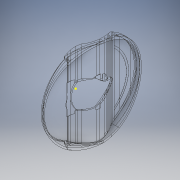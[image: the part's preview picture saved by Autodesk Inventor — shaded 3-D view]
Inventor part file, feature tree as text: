
AUTODESK INVENTOR PART (.ipt)
format: ipt  version: 2018 (Build 220112000, 112)  size: 1,359,360 bytes
history: native  units: mm
features: sketch x50, extrude x43, fillet x2, revolve x1, mirror x1
ambient origin geometry x8: Origin, YZ Plane, XZ Plane, XY Plane, X Axis, Y Axis, Z Axis, Center Point
bodies: Solid1 (feature_tree)
feature tree (97):
  extrude  "Extrusion1"  TaperAngle=0.0deg  [1 undecoded]
  extrude  "Extrusion2"  Depth=10.0mm TaperAngle=0.0deg
  extrude  "Extrusion3"  Depth=10.0mm
  extrude  "Extrusion4"  TaperAngle=0.0deg  [1 undecoded]
  extrude  "Extrusion5"  Depth=10.0mm TaperAngle=0.0deg
  sketch  "Sketch6"  dims[d19=10.0mm d20=0.0mm d21=40.0mm]
  extrude  "Extrusion6"  Depth=10.0mm
  extrude  "Extrusion7"  Depth=11.0mm TaperAngle=0.0deg
  extrude  "Extrusion8"  Depth=32.0mm TaperAngle=0.0deg
  extrude  "Extrusion9"  Depth=32.0mm TaperAngle=0.0deg
  extrude  "Extrusion10"  Depth=10.0mm TaperAngle=0.0deg
  extrude  "Extrusion11"  Depth=10.0mm TaperAngle=0.0deg
  extrude  "Extrusion12"  TaperAngle=0.0deg  [1 undecoded]
  extrude  "Extrusion14"  Depth=48.3mm
  extrude  "Extrusion15"  TaperAngle=0.0deg  [1 undecoded]
  extrude  "Extrusion16"  Depth=10.0mm TaperAngle=0.0deg
  extrude  "Extrusion17"  Depth=11.63mm TaperAngle=0.0deg
  sketch  "Sketch21"  dims[d83=0.0mm d84=0.0mm d85=0.0mm d86=0.0mm]
  extrude  "Extrusion19"  Depth=11.63mm TaperAngle=0.0deg
  extrude  "Extrusion20"  TaperAngle=0.0deg  [1 undecoded]
  extrude  "Extrusion21"  Depth=10.0mm TaperAngle=0.0deg
  extrude  "Extrusion22"  TaperAngle=0.0deg  [1 undecoded]
  extrude  "Extrusion23"  Depth=2.86mm TaperAngle=0.0deg
  extrude  "Extrusion24"  TaperAngle=0.0deg  [1 undecoded]
  extrude  "Extrusion25"  Depth=2.22mm
  sketch  "Sketch33"  dims[d113=7.8mm d114=0.0mm d115=7.8mm d116=0.0mm]
  extrude  "Extrusion26"  Depth=10.0mm TaperAngle=0.0deg
  extrude  "Extrusion27"  Depth=7.8mm TaperAngle=0.0deg
  extrude  "Extrusion28"  Depth=16.0mm TaperAngle=0.0deg
  extrude  "Extrusion29"  [1 undecoded]
  extrude  "Extrusion30"  [1 undecoded]
  extrude  "Extrusion31"  [1 undecoded]
  extrude  "Extrusion32"  [1 undecoded]
  extrude  "Extrusion33"  [1 undecoded]
  sketch  "Sketch42"
  extrude  "Extrusion34"  [1 undecoded]
  extrude  "Extrusion36"  [1 undecoded]
  extrude  "Extrusion37"  [1 undecoded]
  revolve  "Revolution3"  [1 undecoded]
  extrude  "Extrusion38"  [1 undecoded]
  extrude  "Extrusion39"  [1 undecoded]
  extrude  "Extrusion40"  [1 undecoded]
  fillet  "Fillet1"  [1 undecoded]
  fillet  "Fillet2"  [1 undecoded]
  sketch  "Sketch51"
  extrude  "Extrusion41"  [1 undecoded]
  mirror  "Mirror1"
  extrude  "Extrusion42"  [1 undecoded]
  sketch  "Sketch54"
  sketch  "Sketch55"
  sketch  "Sketch56"
  extrude  "Extrusion44"  [1 undecoded]
  extrude  "Extrusion45"  [1 undecoded]
  extrude  "Extrusion46"  [1 undecoded]
  extrude  "Extrusion47"  [1 undecoded]
  sketch  "Sketch1"  dims[d0=10.0mm d1=0.0mm d2=0.0mm d3=0.0mm]
  sketch  "Sketch2"  dims[d4=0.0mm d5=0.0mm d6=10.0mm d7=0.0mm]
  sketch  "Sketch3"  dims[d8=10.0mm d9=0.0mm d10=50.0mm]
  sketch  "Sketch4"  dims[d11=10.0mm d12=0.0mm d13=0.0mm d14=0.0mm]
  sketch  "Sketch5"  dims[d15=0.0mm d16=0.0mm d17=10.0mm d18=0.0mm]
  sketch  "Sketch7"  dims[d22=38.0mm d23=11.0mm d24=0.0mm]
  sketch  "Sketch8"  dims[d25=9.5mm d26=0.0mm d33=32.0mm d34=0.0mm]
  sketch  "Sketch9"  dims[d37=32.0mm d38=0.0mm d39=32.0mm d40=0.0mm]
  sketch  "Sketch10"  dims[d41=32.0mm d42=0.0mm d45=10.0mm d46=0.0mm]
  sketch  "Sketch11"  dims[d47=10.0mm d48=0.0mm d49=10.0mm d50=0.0mm]
  sketch  "Sketch12"  dims[d51=0.0mm d52=0.0mm d53=0.0mm d54=0.0mm]
  sketch  "Sketch13"  dims[d65=46.0mm d66=48.3mm]
  sketch  "Sketch16"  dims[d67=9.0mm d68=0.0mm d69=0.0mm d70=0.0mm]
  sketch  "Sketch18"  dims[d71=0.0mm d72=0.0mm d73=10.0mm d74=0.0mm]
  sketch  "Sketch19"  dims[d75=5.0mm d76=0.0mm d77=11.63mm d78=0.0mm]
  sketch  "Sketch20"  dims[d79=11.63mm d80=0.0mm d81=11.63mm d82=0.0mm]
  sketch  "Sketch22"  dims[d87=30.0mm d88=10.0mm d89=0.0mm]
  sketch  "Sketch23"  dims[d92=10.0mm d93=0.0mm d94=0.0mm d95=0.0mm]
  sketch  "Sketch24"  dims[d96=135.0deg d99=2.86mm d100=0.0mm]
  sketch  "Sketch25"  dims[d101=0.0mm d102=0.0mm d103=0.0mm d104=0.0mm]
  sketch  "Sketch31"  dims[d105=2.01mm d106=2.22mm]
  sketch  "Sketch32"  dims[d107=10.0mm d108=0.0mm d109=10.0mm d110=0.0mm]
  sketch  "Sketch34"  dims[d117=0.0mm d118=0.0mm d119=16.0mm d120=0.0mm]
  sketch  "Sketch35"
  sketch  "Sketch36"
  sketch  "Sketch37"
  sketch  "Sketch38"
  sketch  "Sketch39"
  sketch  "Sketch40"
  sketch  "Sketch41"
  sketch  "Sketch43"
  sketch  "Sketch45"
  sketch  "Sketch47"
  sketch  "Sketch48"
  sketch  "Sketch49"
  sketch  "Sketch50"
  sketch  "Sketch52"
  sketch  "Sketch53"
  sketch  "Sketch57"
  sketch  "Sketch59"
  sketch  "Sketch60"
  sketch  "Sketch61"
note: 27 required parameter values undecoded (feature->parameter linkage not recoverable at this tier; creation-order binding heuristic only, values carry confidence <= 0.55)
